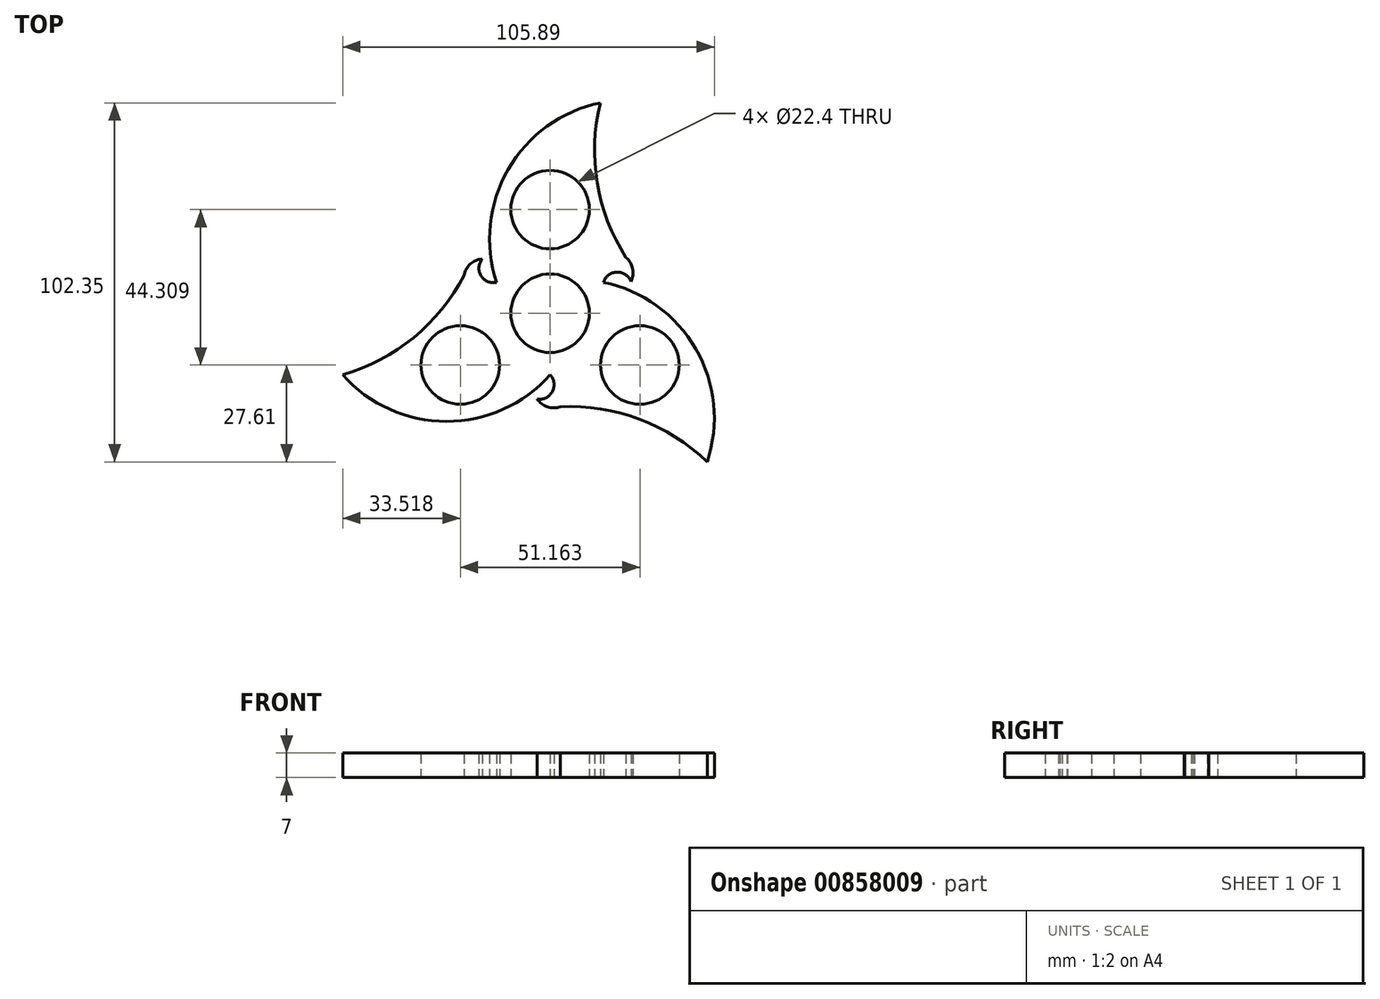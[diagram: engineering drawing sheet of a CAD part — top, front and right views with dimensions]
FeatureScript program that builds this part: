
annotation { "Feature Type Name" : "Feature", "Feature Type Description" : "" }
export const myFeature = defineFeature(function(context is Context, id is Id, definition is map)
    precondition{}
    {
        {
            var Q0;
            Q0=qCreatedBy(makeId("Top.planeOp"),FACE);
            var sketch = newSketch(context, id + "F0", { "sketchPlane" : qUnion([Q0])});
            skCircle(sketch, "E0", {"center": v(0, 0) * mm, "radius": 11.2 * mm});
            skCircle(sketch, "E1", {"center": v(0, 29.54) * mm, "radius": 11.2 * mm});
            skCircle(sketch, "E2.1.1", {"center": v(-25.58, -14.77) * mm, "radius": 11.2 * mm});
            skCircle(sketch, "E2.2.1", {"center": v(25.58, -14.77) * mm, "radius": 11.2 * mm});
            skArc(sketch, "E3", {"start": v(-59.1, -17.59) * mm, "mid": v(-38.9, -6.96) * mm, "end": v(-24.56, 10.8) * mm});
            skArc(sketch, "E4", {"start": v(-59.1, -17.59) * mm, "mid": v(-29.55, -30.86) * mm, "end": v(0, -17.59) * mm});
            skArc(sketch, "E5.1.0", {"start": v(44.78, -42.38) * mm, "mid": v(25.47, -30.2) * mm, "end": v(2.92, -26.67) * mm});
            skArc(sketch, "E5.1.1", {"start": v(44.78, -42.38) * mm, "mid": v(41.5, -10.16) * mm, "end": v(15.23, 8.8) * mm});
            skArc(sketch, "E5.2.0", {"start": v(14.32, 59.97) * mm, "mid": v(13.42, 37.16) * mm, "end": v(21.64, 15.86) * mm});
            skArc(sketch, "E5.2.1", {"start": v(14.32, 59.97) * mm, "mid": v(-11.95, 41.02) * mm, "end": v(-15.23, 8.8) * mm});
            skArc(sketch, "E6", {"start": v(-19.33, 15.45) * mm, "mid": v(-22.74, 14.03) * mm, "end": v(-24.56, 10.8) * mm});
            skArc(sketch, "E7", {"start": v(-19.33, 15.45) * mm, "mid": v(-19.68, 10.65) * mm, "end": v(-15.23, 8.8) * mm});
            skArc(sketch, "E8.1.0", {"start": v(-3.72, -24.47) * mm, "mid": v(-0.78, -26.71) * mm, "end": v(2.92, -26.67) * mm});
            skArc(sketch, "E8.1.1", {"start": v(-3.72, -24.47) * mm, "mid": v(0.62, -22.37) * mm, "end": v(0, -17.59) * mm});
            skArc(sketch, "E8.2.0", {"start": v(23.05, 9.01) * mm, "mid": v(23.52, 12.68) * mm, "end": v(21.64, 15.86) * mm});
            skArc(sketch, "E8.2.1", {"start": v(23.05, 9.01) * mm, "mid": v(19.06, 11.72) * mm, "end": v(15.23, 8.8) * mm});
            skSolve(sketch);
        }
        {
            var Q0;
            Q0=makeQuery(id+"F0.imprint","IMPRINT",FACE,{"disambiguationData":[TD([[makeQuery(id+"F0.imprint","IMPRINT",EDGE,{"derivedFrom":sQuery(id+"F0.wireOp",EDGE,"E0")}),-1.0]])]});
            extrude(context, id + "F1", {"entities" : qUnion([Q0]), "depth" : 7 * mm, "offsetDistance" : 25 * mm});
        }
    });
